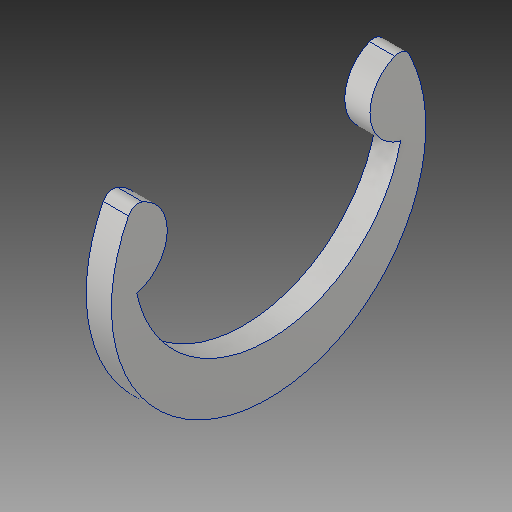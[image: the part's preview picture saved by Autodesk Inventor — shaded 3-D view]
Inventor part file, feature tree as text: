
AUTODESK INVENTOR PART (.ipt)
format: ipt  version: 2017 (Build 210142000, 142)  size: 108,544 bytes
history: native  units: in
note: dims shown in document units (in); Inventor stores cm internally (conversion verified against a paired STEP export)
features: extrude x1
ambient origin geometry x8: Origin, YZ Plane, XZ Plane, XY Plane, X Axis, Y Axis, Z Axis, Center Point
bodies: Solid1 (feature_tree)
feature tree (1):
  extrude  "Extrude1"  [1 undecoded]
note: 1 required parameter value undecoded (feature->parameter linkage not recoverable at this tier; creation-order binding heuristic only, values carry confidence <= 0.55)
